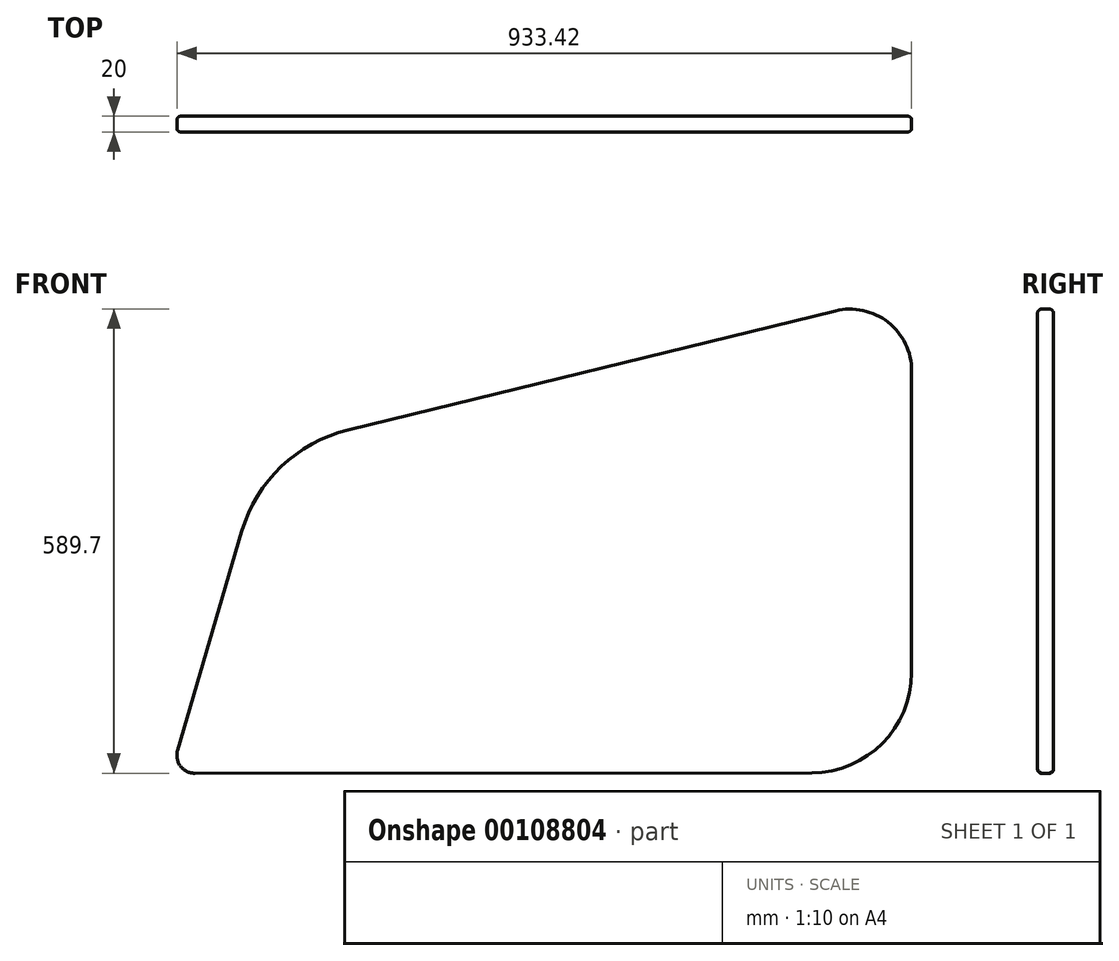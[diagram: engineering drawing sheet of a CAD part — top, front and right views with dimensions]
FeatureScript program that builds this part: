
annotation { "Feature Type Name" : "Feature", "Feature Type Description" : "" }
export const myFeature = defineFeature(function(context is Context, id is Id, definition is map)
    precondition{}
    {
        {
            var Q0;
            Q0=qCreatedBy(makeId("Front.planeOp"),FACE);
            var sketch = newSketch(context, id + "F0", { "sketchPlane" : qUnion([Q0])});
            skLineSegment(sketch, "E0", {"start": v(-111.82, -27.37) * mm, "end": v(-30.29, 250.55) * mm});
            skLineSegment(sketch, "E1", {"start": v(104.5, 379.34) * mm, "end": v(723.62, 530.73) * mm});
            skLineSegment(sketch, "E2", {"start": v(820.67, 454.56) * mm, "end": v(820.67, 71.05) * mm});
            skLineSegment(sketch, "E3", {"start": v(693.76, -55.98) * mm, "end": v(-89.83, -56.72) * mm});
            skPoint(sketch, "E4.visualSharp", {"position": v(0, 353.78) * mm});
            skArc(sketch, "E4.filletArc", {"start": v(104.5, 379.34) * mm, "mid": v(19.88, 332.97) * mm, "end": v(-30.29, 250.55) * mm});
            skPoint(sketch, "E5.visualSharp", {"position": v(-120.44, -56.75) * mm});
            skArc(sketch, "E5.filletArc", {"start": v(-111.82, -27.37) * mm, "mid": v(-108.17, -47.55) * mm, "end": v(-89.83, -56.72) * mm});
            skPoint(sketch, "E6.visualSharp", {"position": v(820.67, -55.86) * mm});
            skArc(sketch, "E6.filletArc", {"start": v(693.76, -55.98) * mm, "mid": v(783.5, -18.73) * mm, "end": v(820.67, 71.05) * mm});
            skPoint(sketch, "E7.visualSharp", {"position": v(820.67, 554.47) * mm});
            skArc(sketch, "E7.filletArc", {"start": v(820.67, 454.56) * mm, "mid": v(790.67, 516.24) * mm, "end": v(723.62, 530.73) * mm});
            skSolve(sketch);
        }
        {
            var Q0;
            Q0=makeQuery(id+"F0.imprint","IMPRINT",FACE,{"disambiguationData":[TD([[makeQuery(id+"F0.imprint","IMPRINT",EDGE,{"derivedFrom":sQuery(id+"F0.wireOp",EDGE,"E0")}),-1.0]])]});
            extrude(context, id + "F1", {"entities" : qUnion([Q0]), "endBound" : BoundingType.SYMMETRIC, "depth" : 20 * mm});
        }
        {
            var Q0;
            Q0=makeQuery(id+"F1.opExtrude","CAP_EDGE",EDGE,{"disambiguationData":[OSD([sQuery(id+"F0.wireOp",EDGE,"E4.filletArc")])],"isStart":false});
            var Q1;
            Q1=makeQuery(id+"F1.opExtrude","CAP_EDGE",EDGE,{"disambiguationData":[OSD([sQuery(id+"F0.wireOp",EDGE,"E1")])],"isStart":false});
            var Q2;
            Q2=makeQuery(id+"F1.opExtrude","CAP_EDGE",EDGE,{"disambiguationData":[OSD([sQuery(id+"F0.wireOp",EDGE,"E7.filletArc")])],"isStart":false});
            var Q3;
            Q3=makeQuery(id+"F1.opExtrude","CAP_EDGE",EDGE,{"disambiguationData":[OSD([sQuery(id+"F0.wireOp",EDGE,"E2")])],"isStart":false});
            var Q4;
            Q4=makeQuery(id+"F1.opExtrude","CAP_EDGE",EDGE,{"disambiguationData":[OSD([sQuery(id+"F0.wireOp",EDGE,"E6.filletArc")])],"isStart":false});
            var Q5;
            Q5=makeQuery(id+"F1.opExtrude","CAP_EDGE",EDGE,{"disambiguationData":[OSD([sQuery(id+"F0.wireOp",EDGE,"E3")])],"isStart":false});
            var Q6;
            Q6=makeQuery(id+"F1.opExtrude","CAP_EDGE",EDGE,{"disambiguationData":[OSD([sQuery(id+"F0.wireOp",EDGE,"E5.filletArc")])],"isStart":true});
            var Q7;
            Q7=makeQuery(id+"F1.opExtrude","CAP_EDGE",EDGE,{"disambiguationData":[OSD([sQuery(id+"F0.wireOp",EDGE,"E0")])],"isStart":false});
            var Q8;
            Q8=makeQuery(id+"F1.opExtrude","CAP_EDGE",EDGE,{"disambiguationData":[OSD([sQuery(id+"F0.wireOp",EDGE,"E0")])],"isStart":true});
            var Q9;
            Q9=makeQuery(id+"F1.opExtrude","CAP_EDGE",EDGE,{"disambiguationData":[OSD([sQuery(id+"F0.wireOp",EDGE,"E4.filletArc")])],"isStart":true});
            var Q10;
            Q10=makeQuery(id+"F1.opExtrude","CAP_EDGE",EDGE,{"disambiguationData":[OSD([sQuery(id+"F0.wireOp",EDGE,"E3")])],"isStart":true});
            fillet(context, id + "F2", {"entities" : qUnion([Q0, Q1, Q2, Q3, Q4, Q5, Q6, Q7, Q8, Q9, Q10]), "radius" : 5 * mm, "tangentPropagation" : true, "allowEdgeOverflow" : false});
        }
    });
